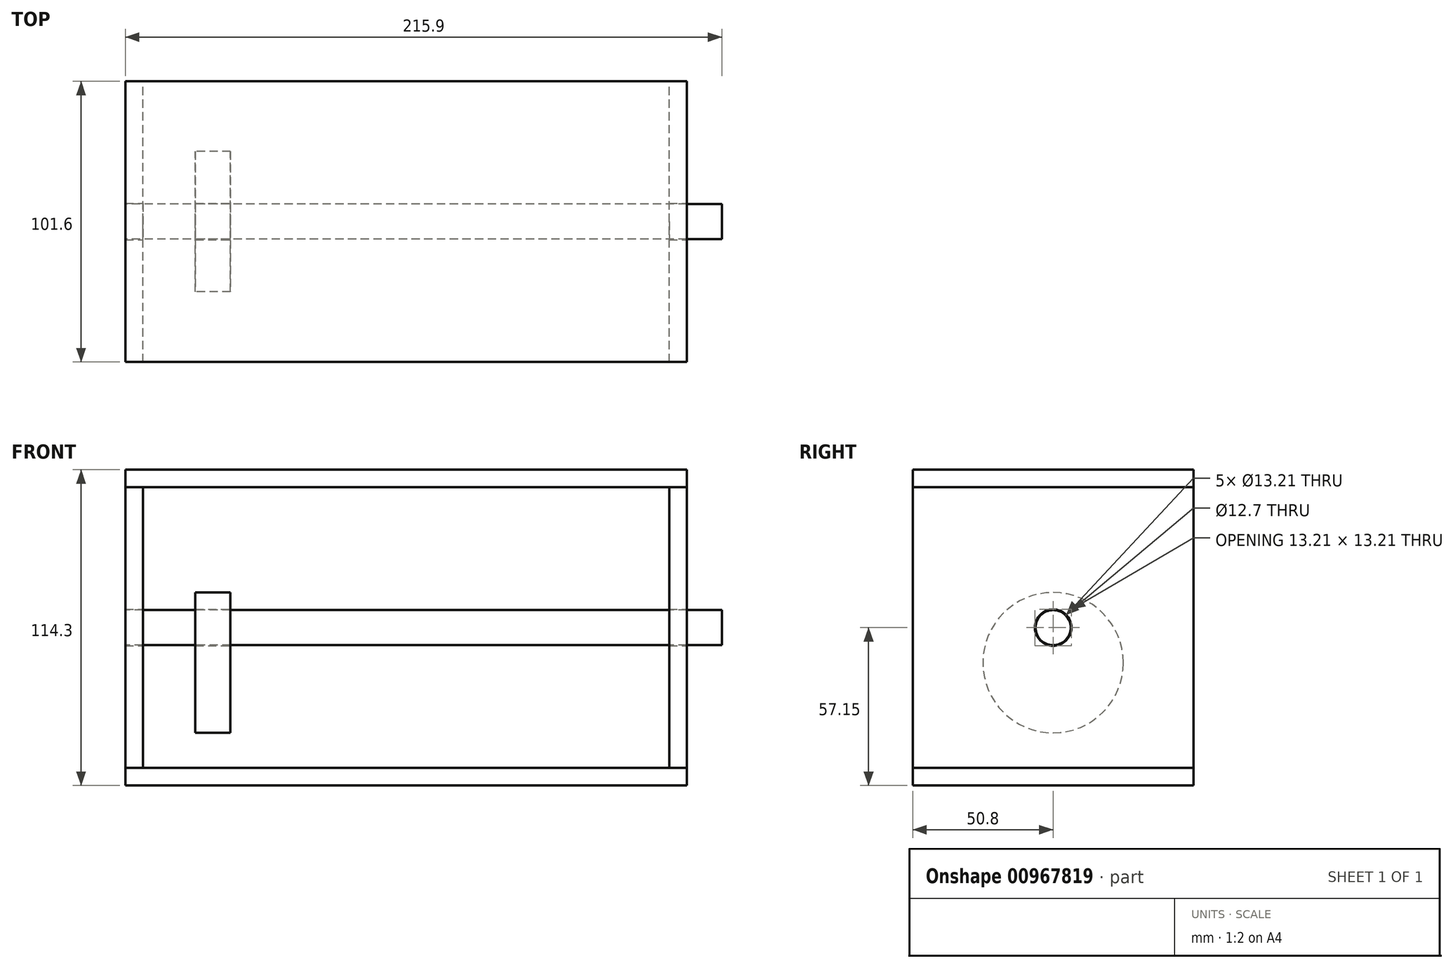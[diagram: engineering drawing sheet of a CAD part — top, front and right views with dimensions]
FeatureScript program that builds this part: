
annotation { "Feature Type Name" : "Feature", "Feature Type Description" : "" }
export const myFeature = defineFeature(function(context is Context, id is Id, definition is map)
    precondition{}
    {
        {
            var Q0;
            Q0=qCreatedBy(makeId("Front.planeOp"),FACE);
            var sketch = newSketch(context, id + "F0", { "sketchPlane" : qUnion([Q0])});
            skLineSegment(sketch, "E0.bottom", {"start": v(-101.6, 6.35) * mm, "end": v(101.6, 6.35) * mm});
            skLineSegment(sketch, "E0.top", {"start": v(-101.6, 0) * mm, "end": v(101.6, 0) * mm});
            skLineSegment(sketch, "E0.left", {"start": v(-101.6, 6.35) * mm, "end": v(-101.6, 0) * mm});
            skLineSegment(sketch, "E0.right", {"start": v(101.6, 6.35) * mm, "end": v(101.6, 0) * mm});
            skLineSegment(sketch, "E1", {"start": v(-101.6, 6.35) * mm, "end": v(-101.6, 107.95) * mm});
            skLineSegment(sketch, "E2", {"start": v(-101.6, 107.95) * mm, "end": v(101.6, 107.95) * mm});
            skLineSegment(sketch, "E3", {"start": v(101.6, 107.95) * mm, "end": v(101.6, 6.35) * mm});
            skLineSegment(sketch, "E4", {"start": v(-95.25, 6.35) * mm, "end": v(-95.25, 107.95) * mm});
            skLineSegment(sketch, "E5", {"start": v(95.25, 6.35) * mm, "end": v(95.25, 107.95) * mm});
            skLineSegment(sketch, "E6", {"start": v(-95.25, 57.15) * mm, "end": v(-101.6, 57.15) * mm, "construction": true});
            skLineSegment(sketch, "E7", {"start": v(95.25, 57.15) * mm, "end": v(101.6, 57.15) * mm, "construction": true});
            skLineSegment(sketch, "E8", {"start": v(-101.6, 107.95) * mm, "end": v(-101.6, 114.3) * mm});
            skLineSegment(sketch, "E9", {"start": v(-101.6, 114.3) * mm, "end": v(101.6, 114.3) * mm});
            skLineSegment(sketch, "E10", {"start": v(101.6, 114.3) * mm, "end": v(101.6, 107.95) * mm});
            skLineSegment(sketch, "E11", {"start": v(-95.25, 57.15) * mm, "end": v(-69.85, 57.15) * mm});
            skLineSegment(sketch, "E12", {"start": v(-69.85, 57.15) * mm, "end": v(0, 57.15) * mm});
            skLineSegment(sketch, "E13", {"start": v(0, 57.15) * mm, "end": v(69.85, 57.15) * mm});
            skLineSegment(sketch, "E14", {"start": v(69.85, 57.15) * mm, "end": v(95.25, 57.15) * mm});
            skLineSegment(sketch, "E15", {"start": v(-69.85, 57.15) * mm, "end": v(-69.85, 44.45) * mm, "construction": true});
            skLineSegment(sketch, "E16", {"start": v(0, 63.5) * mm, "end": v(0, 57.15) * mm, "construction": true});
            skLineSegment(sketch, "E17", {"start": v(69.85, 57.15) * mm, "end": v(69.85, 63.5) * mm, "construction": true});
            skLineSegment(sketch, "E18.bottom", {"start": v(-63.5, 69.85) * mm, "end": v(-76.2, 69.85) * mm});
            skLineSegment(sketch, "E18.top", {"start": v(-63.5, 19.05) * mm, "end": v(-76.2, 19.05) * mm});
            skLineSegment(sketch, "E18.left", {"start": v(-63.5, 69.85) * mm, "end": v(-63.5, 19.05) * mm});
            skLineSegment(sketch, "E18.right", {"start": v(-76.2, 69.85) * mm, "end": v(-76.2, 19.05) * mm});
            skPoint(sketch, "E18.middle", {"position": v(-69.85, 44.45) * mm});
            skLineSegment(sketch, "E19.bottom", {"start": v(6.35, 38.1) * mm, "end": v(-6.35, 38.1) * mm});
            skLineSegment(sketch, "E19.top", {"start": v(6.35, 88.9) * mm, "end": v(-6.35, 88.9) * mm});
            skLineSegment(sketch, "E19.left", {"start": v(6.35, 38.1) * mm, "end": v(6.35, 88.9) * mm});
            skLineSegment(sketch, "E19.right", {"start": v(-6.35, 38.1) * mm, "end": v(-6.35, 88.9) * mm});
            skPoint(sketch, "E19.middle", {"position": v(0, 63.5) * mm});
            skLineSegment(sketch, "E20.bottom", {"start": v(63.5, 38.1) * mm, "end": v(76.2, 38.1) * mm});
            skLineSegment(sketch, "E20.top", {"start": v(63.5, 88.9) * mm, "end": v(76.2, 88.9) * mm});
            skLineSegment(sketch, "E20.left", {"start": v(63.5, 38.1) * mm, "end": v(63.5, 88.9) * mm});
            skLineSegment(sketch, "E20.right", {"start": v(76.2, 38.1) * mm, "end": v(76.2, 88.9) * mm});
            skPoint(sketch, "E20.middle", {"position": v(69.85, 63.5) * mm});
            skLineSegment(sketch, "E21", {"start": v(-76.2, 44.45) * mm, "end": v(-63.5, 44.45) * mm});
            skLineSegment(sketch, "E22", {"start": v(-6.35, 63.5) * mm, "end": v(6.35, 63.5) * mm});
            skLineSegment(sketch, "E23", {"start": v(63.5, 63.5) * mm, "end": v(76.2, 63.5) * mm});
            skLineSegment(sketch, "E24", {"start": v(-69.85, 69.85) * mm, "end": v(-69.85, 133.35) * mm, "construction": true});
            skLineSegment(sketch, "E25", {"start": v(0, 88.9) * mm, "end": v(0, 152.4) * mm, "construction": true});
            skLineSegment(sketch, "E26", {"start": v(69.85, 88.9) * mm, "end": v(69.85, 152.4) * mm, "construction": true});
            skSolve(sketch);
        }
        {
            var Q0;
            Q0=makeQuery(id+"F0.imprint","IMPRINT",FACE,{"disambiguationData":[TD([[makeQuery(id+"F0.imprint","IMPRINT",EDGE,{"derivedFrom":sQuery(id+"F0.wireOp",EDGE,"E0.top")}),1.0]])]});
            var Q1;
            {var subQ0=sQuery(id+"F0.wireOp",EDGE,"E8");Q1=makeQuery(id+"F0.imprint","IMPRINT",FACE,{"disambiguationData":[TD([[makeQuery(id+"F0.imprint","IMPRINT",EDGE,{"derivedFrom":subQ0}),-1.0]])]});}
            extrude(context, id + "F1", {"entities" : qUnion([Q0, Q1]), "endBound" : BoundingType.SYMMETRIC, "depth" : 101.6 * mm, "offsetDistance" : 25.4 * mm});
        }
        {
            var Q0;
            {var subQ1=sQuery(id+"F0.wireOp",EDGE,"E1");Q0=makeQuery(id+"F0.imprint","IMPRINT",FACE,{"disambiguationData":[TD([[makeQuery(id+"F0.imprint","IMPRINT",EDGE,{"derivedFrom":subQ1}),-1.0]])]});}
            var Q1;
            {var subQ4=sQuery(id+"F0.wireOp",EDGE,"E3");Q1=makeQuery(id+"F0.imprint","IMPRINT",FACE,{"disambiguationData":[TD([[makeQuery(id+"F0.imprint","IMPRINT",EDGE,{"derivedFrom":subQ4}),-1.0]])]});}
            var Q2;
            Q2=makeQuery(id+"F1.opExtrude","CAP_FACE",FACE,{"disambiguationData":[OSD([sQuery(id+"F0.wireOp",EDGE,"E2"),sQuery(id+"F0.wireOp",EDGE,"E8"),sQuery(id+"F0.wireOp",EDGE,"E9"),sQuery(id+"F0.wireOp",EDGE,"E10")])],"isStart":false});
            var Q3;
            Q3=makeQuery(id+"F1.opExtrude","CAP_FACE",FACE,{"disambiguationData":[OSD([sQuery(id+"F0.wireOp",EDGE,"E2"),sQuery(id+"F0.wireOp",EDGE,"E8"),sQuery(id+"F0.wireOp",EDGE,"E9"),sQuery(id+"F0.wireOp",EDGE,"E10")])],"isStart":true});
            extrude(context, id + "F2", {"entities" : qUnion([Q0, Q1]), "endBound" : BoundingType.UP_TO_SURFACE, "depth" : 25.4 * mm, "endBoundEntityFace" : qUnion([Q2]), "offsetDistance" : 25.4 * mm, "hasSecondDirection" : true, "secondDirectionBound" : SecondDirectionBoundingType.UP_TO_SURFACE, "secondDirectionOppositeDirection" : true, "secondDirectionDepth" : 25.4 * mm, "secondDirectionBoundEntityFace" : qUnion([Q3])});
        }
        {
            var Q0;
            Q0=makeQuery(id+"F2.opExtrude","SWEPT_FACE",FACE,{"disambiguationData":[OSD([sQuery(id+"F0.wireOp",EDGE,"E3")])]});
            var sketch = newSketch(context, id + "F3", { "sketchPlane" : qUnion([Q0])});
            skCircle(sketch, "E27", {"center": v(0, 57.15) * mm, "radius": 6.6 * mm});
            skCircle(sketch, "E28", {"center": v(0, 57.15) * mm, "radius": 6.35 * mm});
            skSolve(sketch);
        }
        {
            var Q0;
            Q0=makeQuery(id+"F3.imprint","IMPRINT",FACE,{"disambiguationData":[TD([[makeQuery(id+"F3.imprint","IMPRINT",EDGE,{"derivedFrom":sQuery(id+"F3.wireOp",EDGE,"E28")}),1.0]])]});
            var Q1;
            Q1=makeQuery(id+"F3.imprint","IMPRINT",FACE,{"disambiguationData":[TD([[makeQuery(id+"F3.imprint","IMPRINT",EDGE,{"derivedFrom":sQuery(id+"F3.wireOp",EDGE,"E27")}),1.0]])]});
            extrude(context, id + "F4", {"entities" : qUnion([Q0, Q1]), "operationType" : NewBodyOperationType.REMOVE, "endBound" : BoundingType.THROUGH_ALL, "oppositeDirection" : true, "depth" : 25.4 * mm, "offsetDistance" : 25.4 * mm});
        }
        {
            var Q0;
            Q0=makeQuery(id+"F3.imprint","IMPRINT",FACE,{"disambiguationData":[TD([[makeQuery(id+"F3.imprint","IMPRINT",EDGE,{"derivedFrom":sQuery(id+"F3.wireOp",EDGE,"E28")}),1.0]])]});
            var Q1;
            Q1=makeQuery(id+"F2.opExtrude","SWEPT_FACE",FACE,{"disambiguationData":[OSD([sQuery(id+"F0.wireOp",EDGE,"E1")])]});
            extrude(context, id + "F5", {"entities" : qUnion([Q0]), "depth" : 12.7 * mm, "offsetDistance" : 25.4 * mm, "hasSecondDirection" : true, "secondDirectionBound" : SecondDirectionBoundingType.UP_TO_SURFACE, "secondDirectionOppositeDirection" : true, "secondDirectionDepth" : 25.4 * mm, "secondDirectionBoundEntityFace" : qUnion([Q1])});
        }
        {
            var Q0;
            {var subQ0=sQuery(id+"F0.wireOp",EDGE,"E18.top");Q0=makeQuery(id+"F0.imprint","IMPRINT",FACE,{"disambiguationData":[TD([[makeQuery(id+"F0.imprint","IMPRINT",EDGE,{"derivedFrom":subQ0}),-1.0]])]});}
            var Q1;
            Q1=sQuery(id+"F0.wireOp",EDGE,"E21");
            revolve(context, id + "F6", {"surfaceOperationType" : NewSurfaceOperationType.NEW, "entities" : qUnion([Q0]), "axis" : qUnion([Q1]), "revolveType" : RevolveType.FULL});
        }
        {
            var Q0;
            Q0=makeQuery(id+"F5.opExtrude","SWEPT_BODY",BODY,{"disambiguationData":[OSD([sQuery(id+"F3.wireOp",EDGE,"E28")])]});
            var Q1;
            Q1=makeQuery(id+"F6.opRevolve","SWEPT_BODY",BODY,{"disambiguationData":[OSD([sQuery(id+"F0.wireOp",EDGE,"E18.top"),sQuery(id+"F0.wireOp",EDGE,"E18.left"),sQuery(id+"F0.wireOp",EDGE,"E18.right"),sQuery(id+"F0.wireOp",EDGE,"E21")])]});
            booleanBodies(context, id + "F7", {"operationType" : BooleanOperationType.SUBTRACTION, "tools" : qUnion([Q0]), "targets" : qUnion([Q1]), "keepTools" : true});
        }
    });
